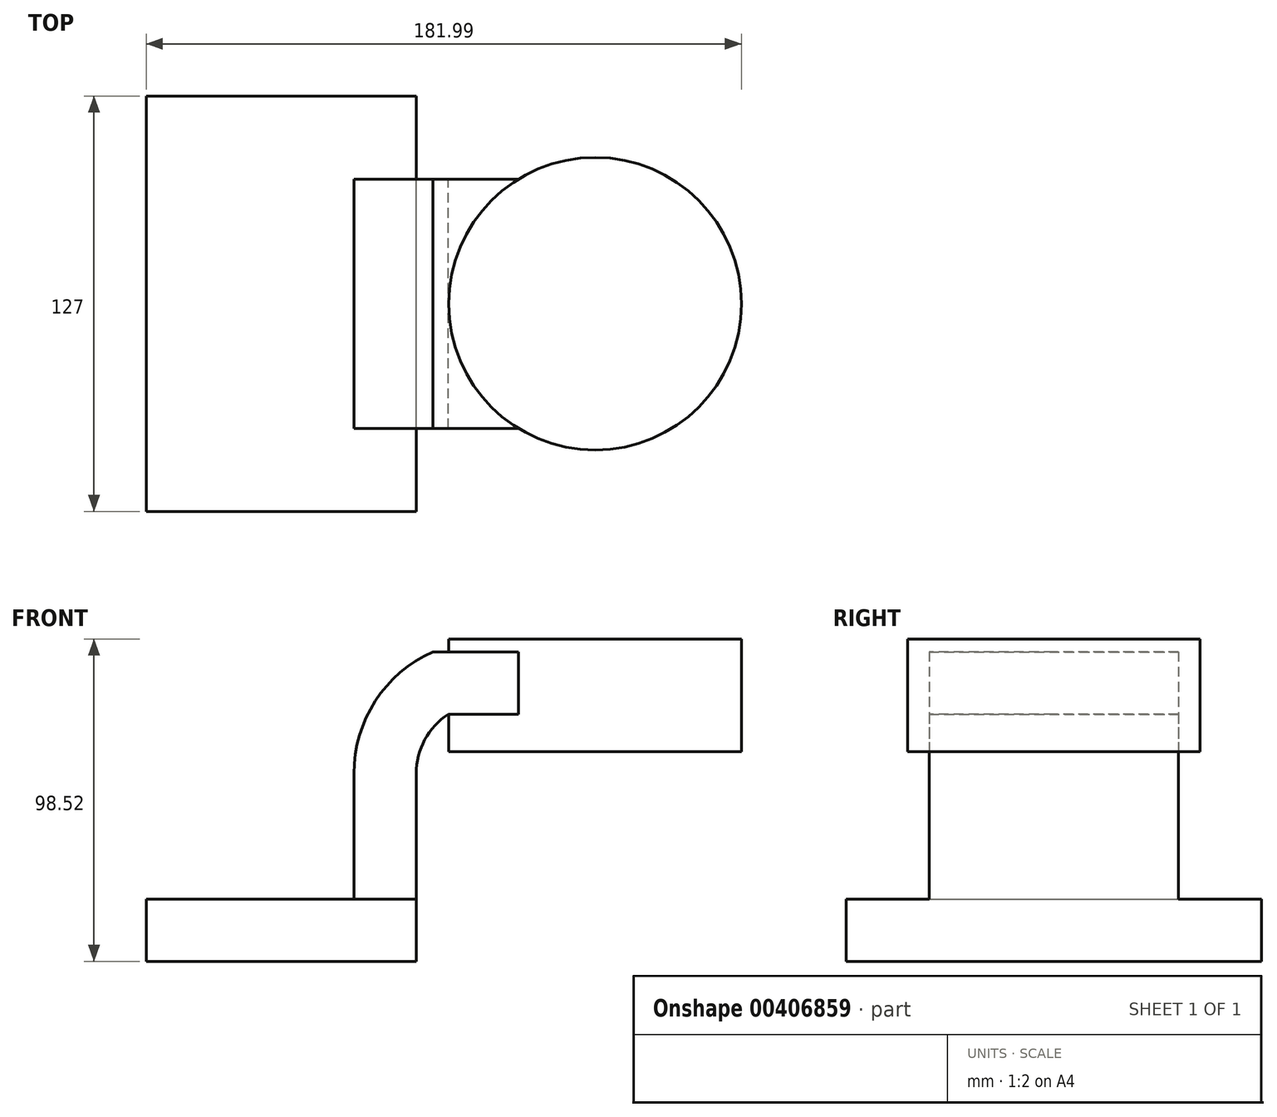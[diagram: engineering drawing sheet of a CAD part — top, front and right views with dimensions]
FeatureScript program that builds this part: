
annotation { "Feature Type Name" : "Feature", "Feature Type Description" : "" }
export const myFeature = defineFeature(function(context is Context, id is Id, definition is map)
    precondition{}
    {
        {
            var Q0;
            Q0=qCreatedBy(makeId("Front.planeOp"),FACE);
            var sketch = newSketch(context, id + "F0", { "sketchPlane" : qUnion([Q0])});
            skLineSegment(sketch, "E0.bottom", {"start": v(-41.28, 9.53) * mm, "end": v(41.28, 9.53) * mm});
            skLineSegment(sketch, "E0.top", {"start": v(-41.28, -9.53) * mm, "end": v(41.28, -9.53) * mm});
            skLineSegment(sketch, "E0.left", {"start": v(-41.28, 9.53) * mm, "end": v(-41.28, -9.53) * mm});
            skLineSegment(sketch, "E0.right", {"start": v(41.28, 9.53) * mm, "end": v(41.28, -9.53) * mm});
            skPoint(sketch, "E0.middle", {"position": v(0, 0) * mm});
            skLineSegment(sketch, "E1.bottom", {"start": v(95.98, 54.51) * mm, "end": v(140.71, 54.51) * mm});
            skLineSegment(sketch, "E1.top", {"start": v(95.98, 89) * mm, "end": v(140.71, 89) * mm});
            skLineSegment(sketch, "E1.left", {"start": v(95.98, 54.51) * mm, "end": v(95.98, 89) * mm});
            skLineSegment(sketch, "E1.right", {"start": v(140.71, 54.51) * mm, "end": v(140.71, 89) * mm});
            skPoint(sketch, "E1.middle", {"position": v(118.35, 71.75) * mm});
            skLineSegment(sketch, "E2", {"start": v(41.28, 9.52) * mm, "end": v(41.28, 47.86) * mm});
            skArc(sketch, "E3", {"start": v(41.28, 47.86) * mm, "mid": v(43.89, 58.2) * mm, "end": v(51.1, 66.03) * mm});
            skLineSegment(sketch, "E4", {"start": v(51.1, 66.03) * mm, "end": v(127.88, 66.03) * mm});
            skLineSegment(sketch, "E5.0", {"start": v(46.35, 85.08) * mm, "end": v(127.88, 85.08) * mm});
            skArc(sketch, "E5.1", {"start": v(22.23, 47.86) * mm, "mid": v(28.78, 70.04) * mm, "end": v(46.35, 85.08) * mm});
            skLineSegment(sketch, "E6", {"start": v(46.35, 85.08) * mm, "end": v(46.35, 85.08) * mm});
            skPoint(sketch, "E7.0.internal.orphan", {"position": v(0, 60.96) * mm});
            skPoint(sketch, "E7.1.internal.orphan", {"position": v(-31.68, 85.08) * mm});
            skFitSpline(sketch, "E8", {"points": [v(-41.28, 9.53) * mm, v(46.35, 85.08) * mm], "startDerivative": vector(104, 30.78) * mm, "endDerivative": vector(139.05, 2.9) * mm});
            skLineSegment(sketch, "E9", {"start": v(22.23, 47.86) * mm, "end": v(22.23, 9.52) * mm});
            skSolve(sketch);
        }
        {
            var Q0;
            Q0=makeQuery(id+"F0.imprint","IMPRINT",FACE,{"disambiguationData":[TD([[makeQuery(id+"F0.imprint","IMPRINT",EDGE,{"derivedFrom":sQuery(id+"F0.wireOp",EDGE,"E0.top")}),1.0]])]});
            extrude(context, id + "F1", {"entities" : qUnion([Q0]), "endBound" : BoundingType.SYMMETRIC, "depth" : 127 * mm});
        }
        {
            var Q0;
            {var subQ1=sQuery(id+"F0.wireOp",EDGE,"E2");Q0=makeQuery(id+"F0.imprint","IMPRINT",FACE,{"disambiguationData":[TD([[makeQuery(id+"F0.imprint","IMPRINT",EDGE,{"derivedFrom":subQ1}),1.0]])]});}
            extrude(context, id + "F2", {"entities" : qUnion([Q0]), "operationType" : NewBodyOperationType.ADD, "endBound" : BoundingType.SYMMETRIC, "depth" : 76.2 * mm});
        }
        {
            var Q0;
            Q0=makeQuery(id+"F0.imprint","IMPRINT",FACE,{"disambiguationData":[TD([[makeQuery(id+"F0.imprint","IMPRINT",EDGE,{"derivedFrom":sQuery(id+"F0.wireOp",EDGE,"E5.1")}),1.0]])]});
            extrude(context, id + "F3", {"entities" : qUnion([Q0]), "operationType" : NewBodyOperationType.ADD, "endBound" : BoundingType.SYMMETRIC, "depth" : 63.5 * mm});
        }
        {
            var Q0;
            {var subQ3=sQuery(id+"F0.wireOp",EDGE,"E1.bottom");Q0=makeQuery(id+"F0.imprint","IMPRINT",FACE,{"disambiguationData":[TD([[makeQuery(id+"F0.imprint","IMPRINT",EDGE,{"derivedFrom":subQ3}),1.0]])]});}
            var Q1;
            Q1=sQuery(id+"F0.wireOp",EDGE,"E1.left");
            revolve(context, id + "F4", {"operationType" : NewBodyOperationType.ADD, "entities" : qUnion([Q0]), "axis" : qUnion([Q1]), "revolveType" : RevolveType.FULL});
        }
    });
